# Revit family: Konsole 27- 18
name_source: partatom
category: HLS-Bauteile
revit_build: Autodesk Revit 2017 (Build: 20190507_1515(x64)
units: mm (PartAtom-declared; Revit-internal decimal feet)

## family parameters
Basisbauteil = Fläche
Beim Laden mit Abzugskörper schneiden = Nein
Bemaßung runder Anschluss = Durchmesser verwenden
Gemeinsam genutzt = Ja
Raumberechnungspunkt = Nein
Teiletyp = Normal

## types (4) — shared parameters
Ausrichtung Platte = längs
Breite Platte = 35 mm  [stored 0.114829 ft]
Breite Profil = 27 mm  [stored 0.0885827 ft]
Fabrikat = MEFA
Firma = MEFA Befestigungs- und Montagesysteme GmbH
Höhe Profil = 18 mm  [stored 0.0590551 ft]
Kurztext1 = Konsole C-Profil 27/18
Lochabstand = 45 mm
Lochdurchmesser = 10.5 mm
Länge Platte = 67 mm
Material = Stahl
Materialname C-Profil = DC01
Materialname Platte = S235JR
Oberflaeche = galvanisch verzinkt
Profil = C-Profil
Stärke Platte = 4 mm  [stored 0.0131234 ft]
Stärke Profil = 1 mm  [stored 0.00328084 ft]
Vorgabe-Ansicht = 1219 mm

## per-type parameters (varying)
| type | Artikelnummer | EAN | Gewicht | Gewicht pro Bauteil | Kurztext2 | Länge Konsole | Schienenlänge | max. zul. Last F1 | max. zul. Last F2 | max. zul. Last q0 |
| Konsole 27- 18 L= 315 Platte längs gvz | 18010315 | 4250928437440 | 0.25 kg | 0.25 kg | L= 315 mm Platte längs gvz | 315 mm  [stored 1.03346 ft] | Montageschiene 27- 18-1,25 für Konsole : C-Profil 27- 18-1,25 L=  315 | 0.05 kip | 0.03 kip | 0.051 kip/ft |
| Konsole 27- 18 L= 262,5 Platte längs gvz | 18010263 | 4250928437433 | 0.22 kg | 0.22 kg | L= 262,5 mm Platte längs gvz | 263 mm | Montageschiene 27- 18-1,25 für Konsole : C-Profil 27- 18-1,25 L=  262,5 | 0.06 kip | 0.03 kip | 0.073 kip/ft |
| Konsole 27- 18 L= 210 Platte längs gvz | 18010210 | 4250928437426 | 0.19 kg | 0.19 kg | L= 210 mm Platte längs gvz | 210 mm  [stored 0.688976 ft] | Montageschiene 27- 18-1,25 für Konsole : C-Profil 27- 18-1,25 L=  210 | 0.08 kip | 0.04 kip | 0.114 kip/ft |
| Konsole 27- 18 L= 157,5 Platte längs gvz | 18010158 | 4250928437419 | 0.16 kg | 0.16 kg | L= 157,5 mm Platte längs gvz | 158 mm | Montageschiene 27- 18-1,25 für Konsole : C-Profil 27- 18-1,25 L=  157,5 | 0.11 kip | 0.05 kip | 0.201 kip/ft |

note: [stored X ft] marks values corroborated as IEEE doubles in the binary element streams (Revit-internal decimal feet)
